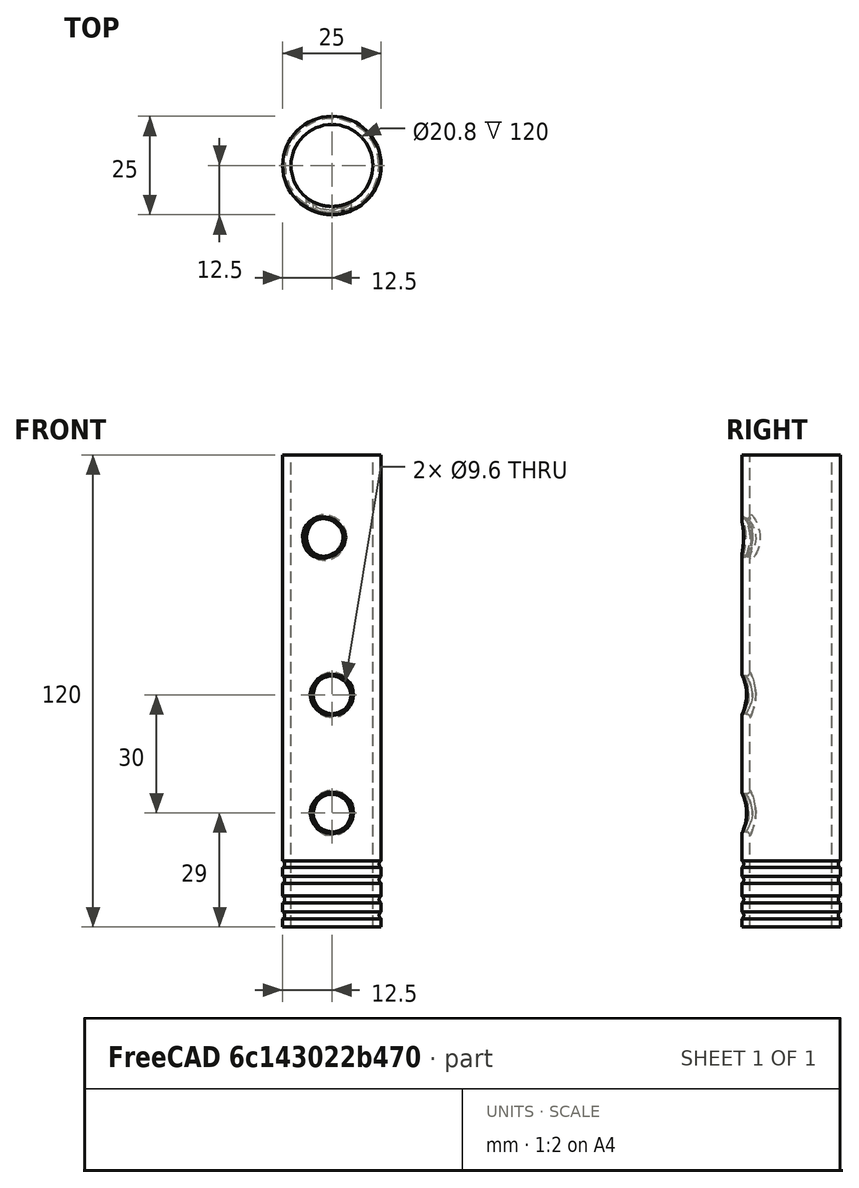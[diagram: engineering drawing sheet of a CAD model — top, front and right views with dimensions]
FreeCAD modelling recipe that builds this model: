
FCSTD DOCUMENT
Label: Part4
License: CC-BY 3.0
LicenseURL: http://creativecommons.org/licenses/by/3.0/
objects: Part::Cut×8, Part::Cylinder×5, Part::Torus×4, PartDesign::Fillet×2
note: 19 computed .brp shape members not serialized (recipe doc carries the construction recipe); baked Part::Feature solids carry a one-line shape summary decoded from their .brp

FEATURE [Part::Torus] Torus001
  Angle1 = -180
  Angle2 = 180
  Angle3 = 360
  Placement = pos=(0,0,16) rot=(0,0,1;0rad)
  Radius1 = 13
  Radius2 = 1
FEATURE [Part::Torus] Torus
  Angle1 = -180
  Angle2 = 180
  Angle3 = 360
  Placement = pos=(0,0,3) rot=(0,0,1;0rad)
  Radius1 = 13
  Radius2 = 1
FEATURE [Part::Cylinder] Cylinder001
  Angle = 360
  Height = 120
  Radius = 10.4
FEATURE [Part::Cylinder] Cylinder
  Angle = 360
  Height = 120
  Radius = 12.5
FEATURE [Part::Cut] Cut
  Base = -> Cylinder
  Tool = -> Cylinder001
FEATURE [Part::Cylinder] Cylinder006  label="Neva"
  Angle = 360
  Height = 10
  Placement = pos=(0,-8,29) rot=(1,0,0;1.5708rad)
  Radius = 4.8
FEATURE [Part::Cylinder] Cylinder006001  label="Nim Hicaz"
  Angle = 360
  Height = 10
  Placement = pos=(0,-8,59) rot=(1,0,0;1.5708rad)
  Radius = 4.8
FEATURE [Part::Cylinder] Cylinder006001001  label="Cargiag"
  Angle = 360
  Height = 10
  Placement = pos=(-1.11338,-7.92214,99) rot=(0.978385,-0.146221,-0.146224;1.5926rad)
  Radius = 4.8
FEATURE [Part::Torus] Torus001001
  Angle1 = -180
  Angle2 = 180
  Angle3 = 360
  Placement = pos=(0,0,12) rot=(0,0,1;0rad)
  Radius1 = 13
  Radius2 = 1
FEATURE [Part::Torus] Torus001002
  Angle1 = -180
  Angle2 = 180
  Angle3 = 360
  Placement = pos=(0,0,7) rot=(0,0,1;0rad)
  Radius1 = 13
  Radius2 = 1
FEATURE [Part::Cut] Cut001
  Base = -> Cut
  Tool = -> Torus001002
FEATURE [Part::Cut] Cut002
  Base = -> Cut001
  Tool = -> Torus001001
FEATURE [Part::Cut] Cut003
  Base = -> Cut002
  Tool = -> Cylinder006001001
FEATURE [Part::Cut] Cut004
  Base = -> Cut003
  Tool = -> Cylinder006001
FEATURE [Part::Cut] Cut005
  Base = -> Cut004
  Tool = -> Cylinder006
FEATURE [Part::Cut] Cut006
  Base = -> Cut005
  Tool = -> Torus001
FEATURE [Part::Cut] Cut007
  Base = -> Cut006
  Tool = -> Torus
FEATURE [PartDesign::Fillet] Fillet
  Base = -> Cut007 [Edge22,Edge21,Edge20]
  Radius = 0.5
FEATURE [PartDesign::Fillet] Fillet001
  Base = -> Fillet [Edge22,Edge23,Edge17]
  Radius = 1
